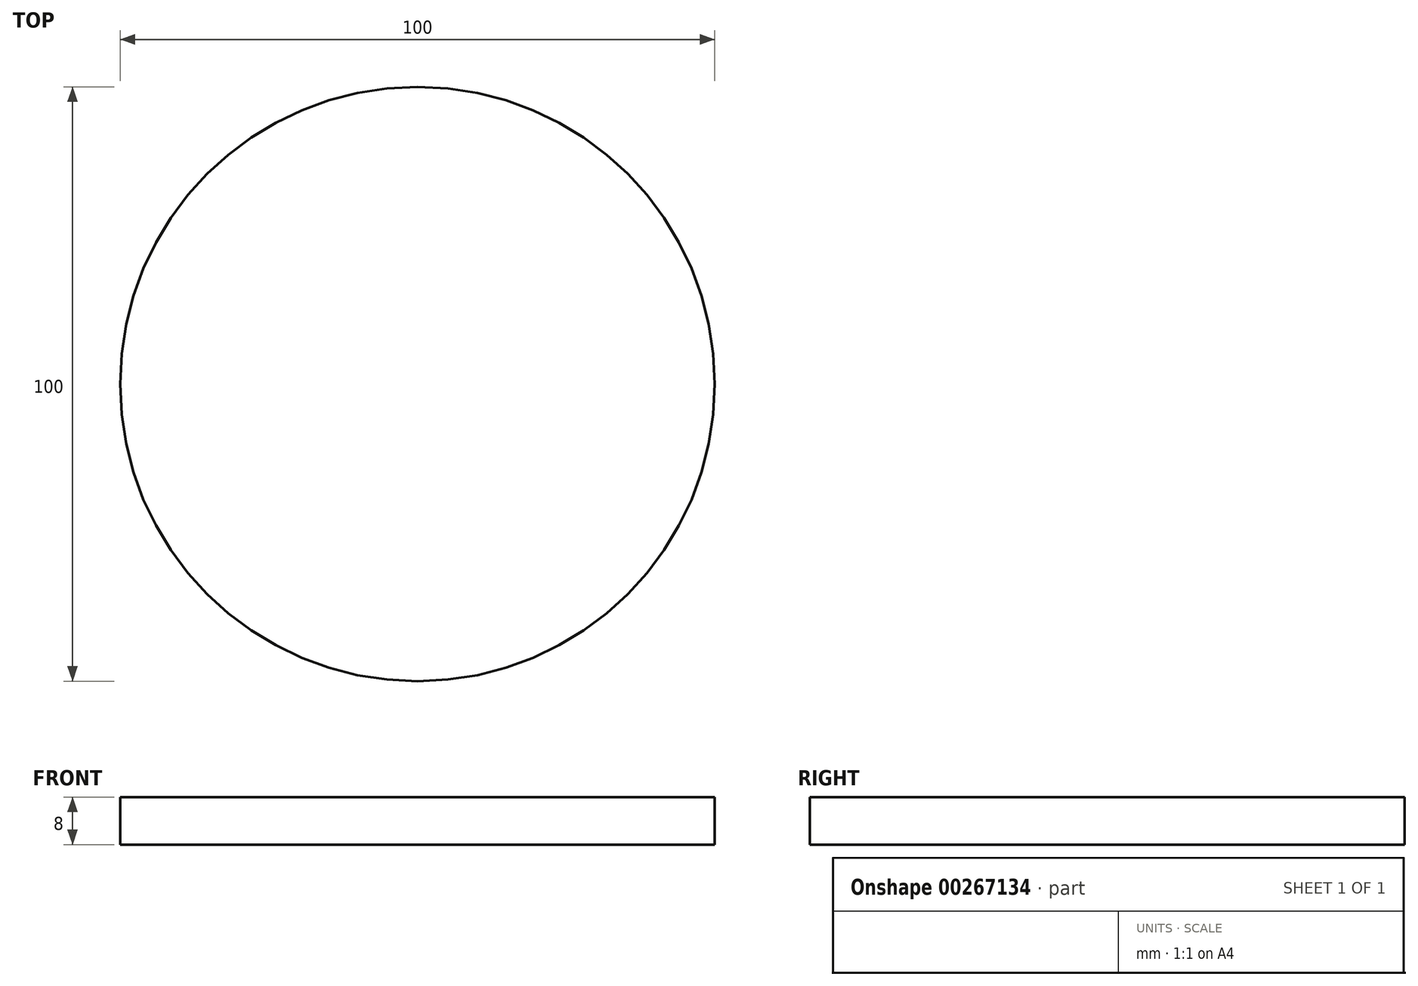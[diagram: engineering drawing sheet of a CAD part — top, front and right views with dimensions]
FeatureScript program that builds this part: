
annotation { "Feature Type Name" : "Feature", "Feature Type Description" : "" }
export const myFeature = defineFeature(function(context is Context, id is Id, definition is map)
    precondition{}
    {
        {
            var Q0;
            Q0=qCreatedBy(makeId("Top.planeOp"),FACE);
            var sketch = newSketch(context, id + "F0", { "sketchPlane" : qUnion([Q0])});
            skCircle(sketch, "E0", {"center": v(0, 0) * mm, "radius": 50 * mm});
            skSolve(sketch);
        }
        {
            var Q0;
            Q0=makeQuery(id+"F0.imprint","IMPRINT",FACE,{"disambiguationData":[TD([[makeQuery(id+"F0.imprint","IMPRINT",EDGE,{"derivedFrom":sQuery(id+"F0.wireOp",EDGE,"E0")}),1.0]])]});
            extrude(context, id + "F1", {"entities" : qUnion([Q0]), "depth" : 8 * mm});
        }
    });
